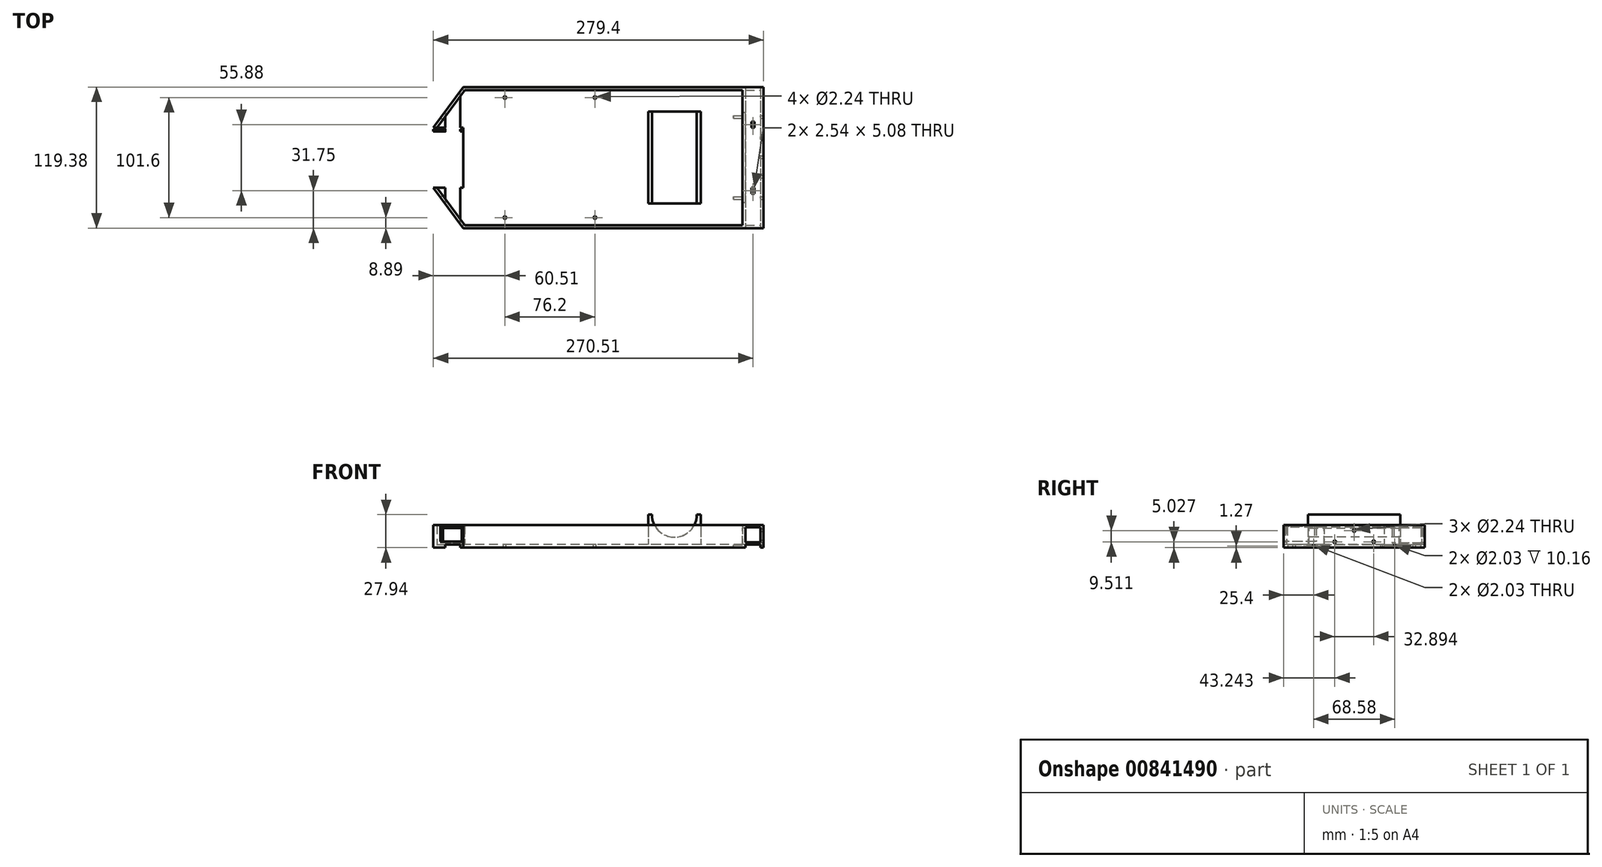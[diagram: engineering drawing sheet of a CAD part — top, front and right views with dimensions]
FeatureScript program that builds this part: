
annotation { "Feature Type Name" : "Feature", "Feature Type Description" : "" }
export const myFeature = defineFeature(function(context is Context, id is Id, definition is map)
    precondition{}
    {
        {
            var Q0;
            Q0=qCreatedBy(makeId("Top.planeOp"),FACE);
            var sketch = newSketch(context, id + "F0", { "sketchPlane" : qUnion([Q0])});
            skLineSegment(sketch, "E0.bottom", {"start": v(127, -59.69) * mm, "end": v(-127, -59.7) * mm});
            skLineSegment(sketch, "E0.top", {"start": v(127, 59.7) * mm, "end": v(-127, 59.69) * mm});
            skLineSegment(sketch, "E0.left", {"start": v(127, -59.69) * mm, "end": v(127, 59.7) * mm});
            skLineSegment(sketch, "E0.right", {"start": v(-127, -59.7) * mm, "end": v(-127, 59.69) * mm});
            skPoint(sketch, "E0.middle", {"position": v(0, 0) * mm});
            skLineSegment(sketch, "E1", {"start": v(-152.4, 25.4) * mm, "end": v(-152.4, -25.4) * mm});
            skLineSegment(sketch, "E2", {"start": v(-152.4, 25.4) * mm, "end": v(-127, 59.69) * mm});
            skLineSegment(sketch, "E3", {"start": v(-152.4, -25.4) * mm, "end": v(-127, -59.7) * mm});
            skSolve(sketch);
        }
        {
            var Q0;
            Q0 = qSketchRegion(id + "F0", true);
            extrude(context, id + "F1", {"entities" : qUnion([Q0]), "depth" : 19.05 * mm, "offsetDistance" : 25.4 * mm});
        }
        {
            var Q0;
            Q0=makeQuery(id+"F1.opExtrude","CAP_FACE",FACE,{"disambiguationData":[OSD([sQuery(id+"F0.wireOp",EDGE,"E0.bottom"),sQuery(id+"F0.wireOp",EDGE,"E0.top"),sQuery(id+"F0.wireOp",EDGE,"E0.left"),sQuery(id+"F0.wireOp",EDGE,"E1"),sQuery(id+"F0.wireOp",EDGE,"E2"),sQuery(id+"F0.wireOp",EDGE,"E3")])],"isStart":false});
            shell(context, id + "F2", {"entities" : qUnion([Q0]), "thickness" : 2.54 * mm});
        }
        {
            var Q0;
            Q0=makeQuery(id+"F1.opExtrude","SWEPT_FACE",FACE,{"disambiguationData":[OSD([sQuery(id+"F0.wireOp",EDGE,"E3")])]});
            var sketch = newSketch(context, id + "F3", { "sketchPlane" : qUnion([Q0])});
            skLineSegment(sketch, "E4.bottom", {"start": v(-60.14, 17.78) * mm, "end": v(-29.66, 17.78) * mm});
            skLineSegment(sketch, "E4.top", {"start": v(-60.14, 5.08) * mm, "end": v(-29.66, 5.08) * mm});
            skLineSegment(sketch, "E4.left", {"start": v(-60.14, 17.78) * mm, "end": v(-60.14, 5.08) * mm});
            skLineSegment(sketch, "E4.right", {"start": v(-29.66, 17.78) * mm, "end": v(-29.66, 5.08) * mm});
            skSolve(sketch);
        }
        {
            var Q0;
            Q0 = qSketchRegion(id + "F3", true);
            extrude(context, id + "F4", {"entities" : qUnion([Q0]), "operationType" : NewBodyOperationType.REMOVE, "oppositeDirection" : true, "depth" : 2.54 * mm, "offsetDistance" : 25.4 * mm});
        }
        {
            var Q0;
            Q0=makeQuery(id+"F1.opExtrude","CAP_FACE",FACE,{"disambiguationData":[OSD([sQuery(id+"F0.wireOp",EDGE,"E0.bottom"),sQuery(id+"F0.wireOp",EDGE,"E0.top"),sQuery(id+"F0.wireOp",EDGE,"E0.left"),sQuery(id+"F0.wireOp",EDGE,"E1"),sQuery(id+"F0.wireOp",EDGE,"E2"),sQuery(id+"F0.wireOp",EDGE,"E3")])],"isStart":true});
            var sketch = newSketch(context, id + "F5", { "sketchPlane" : qUnion([Q0])});
            skLineSegment(sketch, "E5", {"start": v(-129.54, 56.26) * mm, "end": v(-129.54, -56.26) * mm});
            skLineSegment(sketch, "E6", {"start": v(-142.24, -39.12) * mm, "end": v(-142.24, 39.12) * mm});
            skLineSegment(sketch, "E7", {"start": v(-129.54, -56.26) * mm, "end": v(-142.24, -39.12) * mm});
            skLineSegment(sketch, "E8", {"start": v(-142.24, 39.12) * mm, "end": v(-129.54, 56.26) * mm});
            skLineSegment(sketch, "E9.bottom", {"start": v(124.46, -59.7) * mm, "end": v(111.76, -59.7) * mm});
            skLineSegment(sketch, "E9.top", {"start": v(124.46, 59.7) * mm, "end": v(111.76, 59.69) * mm});
            skLineSegment(sketch, "E9.left", {"start": v(124.46, -59.7) * mm, "end": v(124.46, 59.7) * mm});
            skLineSegment(sketch, "E9.right", {"start": v(111.76, -59.7) * mm, "end": v(111.76, 59.69) * mm});
            skSolve(sketch);
        }
        {
            var Q0;
            Q0=makeQuery(id+"F5.imprint","IMPRINT",FACE,{"disambiguationData":[TD([[makeQuery(id+"F5.imprint","IMPRINT",EDGE,{"derivedFrom":sQuery(id+"F5.wireOp",EDGE,"E5")}),-1.0]])]});
            var Q1;
            Q1=makeQuery(id+"F5.imprint","IMPRINT",FACE,{"disambiguationData":[TD([[makeQuery(id+"F5.imprint","IMPRINT",EDGE,{"derivedFrom":sQuery(id+"F5.wireOp",EDGE,"E9.bottom")}),-1.0]])]});
            extrude(context, id + "F6", {"entities" : qUnion([Q0, Q1]), "operationType" : NewBodyOperationType.REMOVE, "oppositeDirection" : true, "depth" : 2.54 * mm, "offsetDistance" : 25.4 * mm});
        }
        {
            var Q0;
            Q0=makeQuery(id+"F1.opExtrude","SWEPT_FACE",FACE,{"disambiguationData":[OSD([sQuery(id+"F0.wireOp",EDGE,"E1")])]});
            var sketch = newSketch(context, id + "F7", { "sketchPlane" : qUnion([Q0])});
            skCircle(sketch, "E10", {"center": v(23.11, 1.27) * mm, "radius": 1.02 * mm});
            skCircle(sketch, "E11.MirrorC", {"center": v(-23.11, 1.27) * mm, "radius": 1.02 * mm});
            skSolve(sketch);
        }
        {
            var Q0;
            Q0=makeQuery(id+"F7.imprint","IMPRINT",FACE,{"disambiguationData":[TD([[makeQuery(id+"F7.imprint","IMPRINT",EDGE,{"derivedFrom":sQuery(id+"F7.wireOp",EDGE,"E11.MirrorC")}),-1.0]])]});
            var Q1;
            Q1=makeQuery(id+"F7.imprint","IMPRINT",FACE,{"disambiguationData":[TD([[makeQuery(id+"F7.imprint","IMPRINT",EDGE,{"derivedFrom":sQuery(id+"F7.wireOp",EDGE,"E10")}),1.0]])]});
            extrude(context, id + "F8", {"entities" : qUnion([Q0, Q1]), "operationType" : NewBodyOperationType.REMOVE, "oppositeDirection" : true, "depth" : 25.4 * mm, "offsetDistance" : 25.4 * mm});
        }
        {
            var Q0;
            Q0=makeQuery(id+"F1.opExtrude","SWEPT_FACE",FACE,{"disambiguationData":[OSD([sQuery(id+"F0.wireOp",EDGE,"E0.left")])]});
            var sketch = newSketch(context, id + "F9", { "sketchPlane" : qUnion([Q0])});
            skCircle(sketch, "E12", {"center": v(-34.29, 1.27) * mm, "radius": 1.02 * mm});
            skCircle(sketch, "E13.MirrorC", {"center": v(34.29, 1.27) * mm, "radius": 1.02 * mm});
            skSolve(sketch);
        }
        {
            var Q0;
            Q0 = qSketchRegion(id + "F9", true);
            extrude(context, id + "F10", {"entities" : qUnion([Q0]), "operationType" : NewBodyOperationType.REMOVE, "oppositeDirection" : true, "depth" : 25.4 * mm, "offsetDistance" : 25.4 * mm});
        }
        {
            var Q0;
            Q0=makeQuery(id+"F1.opExtrude","SWEPT_FACE",FACE,{"disambiguationData":[OSD([sQuery(id+"F0.wireOp",EDGE,"E2")])]});
            var sketch = newSketch(context, id + "F11", { "sketchPlane" : qUnion([Q0])});
            skLineSegment(sketch, "E14.bottom", {"start": v(29.66, 16.51) * mm, "end": v(60.14, 16.51) * mm});
            skLineSegment(sketch, "E14.top", {"start": v(29.66, 3.81) * mm, "end": v(60.14, 3.81) * mm});
            skLineSegment(sketch, "E14.left", {"start": v(29.66, 16.51) * mm, "end": v(29.66, 3.81) * mm});
            skLineSegment(sketch, "E14.right", {"start": v(60.14, 16.51) * mm, "end": v(60.14, 3.81) * mm});
            skSolve(sketch);
        }
        {
            var Q0;
            Q0 = qSketchRegion(id + "F11", true);
            extrude(context, id + "F12", {"entities" : qUnion([Q0]), "operationType" : NewBodyOperationType.REMOVE, "oppositeDirection" : true, "depth" : 2.54 * mm, "offsetDistance" : 25.4 * mm});
        }
        {
            var Q0;
            Q0=makeQuery(id+"F1.opExtrude","SWEPT_FACE",FACE,{"disambiguationData":[OSD([sQuery(id+"F0.wireOp",EDGE,"E0.bottom")])]});
            var sketch = newSketch(context, id + "F13", { "sketchPlane" : qUnion([Q0])});
            skLineSegment(sketch, "E15.bottom", {"start": v(111.76, 4.45) * mm, "end": v(124.46, 4.45) * mm});
            skLineSegment(sketch, "E15.top", {"start": v(111.76, 17.14) * mm, "end": v(124.46, 17.14) * mm});
            skLineSegment(sketch, "E15.left", {"start": v(111.76, 4.45) * mm, "end": v(111.76, 17.15) * mm});
            skLineSegment(sketch, "E15.right", {"start": v(124.46, 4.45) * mm, "end": v(124.46, 17.14) * mm});
            skSolve(sketch);
        }
        {
            var Q0;
            Q0 = qSketchRegion(id + "F13", true);
            extrude(context, id + "F14", {"entities" : qUnion([Q0]), "operationType" : NewBodyOperationType.REMOVE, "oppositeDirection" : true, "depth" : 101.6 * mm, "offsetDistance" : 25.4 * mm});
        }
        {
            var Q0;
            Q0=qCreatedBy(makeId("Right.planeOp"),FACE);
            var sketch = newSketch(context, id + "F15", { "sketchPlane" : qUnion([Q0])});
            skCircle(sketch, "E16", {"center": v(0, 11.81) * mm, "radius": 1.12 * mm});
            skCircle(sketch, "E17", {"center": v(-17.78, 5.08) * mm, "radius": 1.12 * mm});
            skCircle(sketch, "E18", {"center": v(17.78, 5.08) * mm, "radius": 1.12 * mm});
            skSolve(sketch);
        }
        {
            var Q0;
            Q0 = qSketchRegion(id + "F15", true);
            extrude(context, id + "F16", {"entities" : qUnion([Q0]), "operationType" : NewBodyOperationType.REMOVE, "endBound" : BoundingType.SYMMETRIC, "oppositeDirection" : true, "depth" : 169.16 * mm, "offsetDistance" : 25.4 * mm});
        }
        {
            var Q0;
            Q0=makeQuery(id+"F1.opExtrude","SWEPT_FACE",FACE,{"disambiguationData":[OSD([sQuery(id+"F0.wireOp",EDGE,"E1")])]});
            var sketch = newSketch(context, id + "F17", { "sketchPlane" : qUnion([Q0])});
            skCircle(sketch, "E19", {"center": v(-16.45, 5.03) * mm, "radius": 1.12 * mm});
            skCircle(sketch, "E20", {"center": v(16.45, 5.03) * mm, "radius": 1.12 * mm});
            skCircle(sketch, "E21", {"center": v(0, 14.54) * mm, "radius": 1.12 * mm});
            skSolve(sketch);
        }
        {
            var Q0;
            Q0 = qSketchRegion(id + "F17", true);
            extrude(context, id + "F18", {"entities" : qUnion([Q0]), "operationType" : NewBodyOperationType.REMOVE, "oppositeDirection" : true, "depth" : 279.4 * mm, "offsetDistance" : 25.4 * mm});
        }
        {
            var Q0;
            {var subQ0=sQuery(id+"F0.wireOp",EDGE,"E3");var subQ3=sQuery(id+"F0.wireOp",EDGE,"E0.top");var subQ4=sQuery(id+"F0.wireOp",EDGE,"E2");var subQ5=sQuery(id+"F0.wireOp",EDGE,"E0.bottom");Q0=makeQuery(id+"F6.boolean.opBoolean","SPLIT",FACE,{"disambiguationData":[TD([makeQuery(id+"F2.opShell","OFFSET_FACE",FACE,{"disambiguationData":[OSD([subQ5])]})])],"derivedFrom":makeQuery(id+"F2.opShell","OFFSET_FACE",FACE,{"disambiguationData":[OSD([subQ5,subQ3,sQuery(id+"F0.wireOp",EDGE,"E0.left"),sQuery(id+"F0.wireOp",EDGE,"E1"),subQ4,subQ0])]})});}
            var sketch = newSketch(context, id + "F19", { "sketchPlane" : qUnion([Q0])});
            skLineSegment(sketch, "E22.bottom", {"start": v(-15.7, -50.8) * mm, "end": v(-91.9, -50.8) * mm});
            skLineSegment(sketch, "E22.top", {"start": v(-15.7, 50.8) * mm, "end": v(-91.9, 50.8) * mm});
            skLineSegment(sketch, "E22.left", {"start": v(-15.7, -50.8) * mm, "end": v(-15.7, 50.8) * mm});
            skLineSegment(sketch, "E22.right", {"start": v(-91.9, -50.8) * mm, "end": v(-91.9, 50.8) * mm});
            skPoint(sketch, "E22.middle", {"position": v(-53.8, 0) * mm});
            skCircle(sketch, "E23", {"center": v(-91.9, 50.8) * mm, "radius": 1.12 * mm});
            skCircle(sketch, "E24", {"center": v(-15.7, 50.8) * mm, "radius": 1.12 * mm});
            skCircle(sketch, "E25", {"center": v(-15.7, -50.8) * mm, "radius": 1.12 * mm});
            skCircle(sketch, "E26", {"center": v(-91.9, -50.8) * mm, "radius": 1.12 * mm});
            skSolve(sketch);
        }
        {
            var Q0;
            {var subQ0=sQuery(id+"F19.wireOp",EDGE,"E22.right");var subQ1=sQuery(id+"F19.wireOp",EDGE,"E22.bottom");var subQ2=makeQuery(id+"F19.imprint","INTERSECT",VERTEX,{"derivedFrom":[subQ1,subQ0]});Q0=makeQuery(id+"F19.imprint","IMPRINT",FACE,{"disambiguationData":[TD([[makeQuery(id+"F19.imprint","IMPRINT",EDGE,{"disambiguationData":[TD([[subQ2,1.0]])],"derivedFrom":subQ1}),-1.0]])]});}
            var Q1;
            {var subQ0=sQuery(id+"F19.wireOp",EDGE,"E22.right");var subQ1=sQuery(id+"F19.wireOp",EDGE,"E22.bottom");var subQ2=makeQuery(id+"F19.imprint","INTERSECT",VERTEX,{"derivedFrom":[subQ1,subQ0]});Q1=makeQuery(id+"F19.imprint","IMPRINT",FACE,{"disambiguationData":[TD([[makeQuery(id+"F19.imprint","IMPRINT",EDGE,{"disambiguationData":[TD([[subQ2,1.0]])],"derivedFrom":subQ1}),1.0]])]});}
            var Q2;
            {var subQ0=sQuery(id+"F19.wireOp",EDGE,"E22.left");var subQ1=sQuery(id+"F19.wireOp",EDGE,"E22.bottom");var subQ2=makeQuery(id+"F19.imprint","INTERSECT",VERTEX,{"derivedFrom":[subQ1,subQ0]});Q2=makeQuery(id+"F19.imprint","IMPRINT",FACE,{"disambiguationData":[TD([[makeQuery(id+"F19.imprint","IMPRINT",EDGE,{"disambiguationData":[TD([[subQ2,-1.0]])],"derivedFrom":subQ1}),1.0]])]});}
            var Q3;
            {var subQ0=sQuery(id+"F19.wireOp",EDGE,"E22.left");var subQ1=sQuery(id+"F19.wireOp",EDGE,"E22.bottom");var subQ2=makeQuery(id+"F19.imprint","INTERSECT",VERTEX,{"derivedFrom":[subQ1,subQ0]});Q3=makeQuery(id+"F19.imprint","IMPRINT",FACE,{"disambiguationData":[TD([[makeQuery(id+"F19.imprint","IMPRINT",EDGE,{"disambiguationData":[TD([[subQ2,-1.0]])],"derivedFrom":subQ1}),-1.0]])]});}
            var Q4;
            {var subQ0=sQuery(id+"F19.wireOp",EDGE,"E22.left");var subQ1=sQuery(id+"F19.wireOp",EDGE,"E22.top");var subQ2=makeQuery(id+"F19.imprint","INTERSECT",VERTEX,{"derivedFrom":[subQ1,subQ0]});Q4=makeQuery(id+"F19.imprint","IMPRINT",FACE,{"disambiguationData":[TD([[makeQuery(id+"F19.imprint","IMPRINT",EDGE,{"disambiguationData":[TD([[subQ2,-1.0]])],"derivedFrom":subQ1}),-1.0]])]});}
            var Q5;
            {var subQ0=sQuery(id+"F19.wireOp",EDGE,"E22.left");var subQ1=sQuery(id+"F19.wireOp",EDGE,"E22.top");var subQ2=makeQuery(id+"F19.imprint","INTERSECT",VERTEX,{"derivedFrom":[subQ1,subQ0]});Q5=makeQuery(id+"F19.imprint","IMPRINT",FACE,{"disambiguationData":[TD([[makeQuery(id+"F19.imprint","IMPRINT",EDGE,{"disambiguationData":[TD([[subQ2,-1.0]])],"derivedFrom":subQ1}),1.0]])]});}
            var Q6;
            {var subQ0=sQuery(id+"F19.wireOp",EDGE,"E22.right");var subQ1=sQuery(id+"F19.wireOp",EDGE,"E22.top");var subQ2=makeQuery(id+"F19.imprint","INTERSECT",VERTEX,{"derivedFrom":[subQ1,subQ0]});Q6=makeQuery(id+"F19.imprint","IMPRINT",FACE,{"disambiguationData":[TD([[makeQuery(id+"F19.imprint","IMPRINT",EDGE,{"disambiguationData":[TD([[subQ2,1.0]])],"derivedFrom":subQ1}),-1.0]])]});}
            var Q7;
            {var subQ0=sQuery(id+"F19.wireOp",EDGE,"E22.right");var subQ1=sQuery(id+"F19.wireOp",EDGE,"E22.top");var subQ2=makeQuery(id+"F19.imprint","INTERSECT",VERTEX,{"derivedFrom":[subQ1,subQ0]});Q7=makeQuery(id+"F19.imprint","IMPRINT",FACE,{"disambiguationData":[TD([[makeQuery(id+"F19.imprint","IMPRINT",EDGE,{"disambiguationData":[TD([[subQ2,1.0]])],"derivedFrom":subQ1}),1.0]])]});}
            extrude(context, id + "F20", {"entities" : qUnion([Q0, Q1, Q2, Q3, Q4, Q5, Q6, Q7]), "operationType" : NewBodyOperationType.REMOVE, "oppositeDirection" : true, "depth" : 2.54 * mm, "offsetDistance" : 25.4 * mm});
        }
        {
            var Q0;
            {var subQ0=sQuery(id+"F0.wireOp",EDGE,"E3");var subQ3=sQuery(id+"F0.wireOp",EDGE,"E0.top");var subQ4=sQuery(id+"F0.wireOp",EDGE,"E2");var subQ5=sQuery(id+"F0.wireOp",EDGE,"E0.bottom");Q0=makeQuery(id+"F6.boolean.opBoolean","SPLIT",FACE,{"disambiguationData":[TD([makeQuery(id+"F2.opShell","OFFSET_FACE",FACE,{"disambiguationData":[OSD([subQ5])]})])],"derivedFrom":makeQuery(id+"F2.opShell","OFFSET_FACE",FACE,{"disambiguationData":[OSD([subQ5,subQ3,sQuery(id+"F0.wireOp",EDGE,"E0.left"),sQuery(id+"F0.wireOp",EDGE,"E1"),subQ4,subQ0])]})});}
            var sketch = newSketch(context, id + "F21", { "sketchPlane" : qUnion([Q0])});
            skLineSegment(sketch, "E27.bottom", {"start": v(73.76, -38.99) * mm, "end": v(29.31, -38.99) * mm});
            skLineSegment(sketch, "E27.top", {"start": v(73.76, 38.99) * mm, "end": v(29.31, 38.99) * mm});
            skLineSegment(sketch, "E27.left", {"start": v(73.76, -38.99) * mm, "end": v(73.76, 38.99) * mm});
            skLineSegment(sketch, "E27.right", {"start": v(29.31, -38.99) * mm, "end": v(29.31, 38.99) * mm});
            skPoint(sketch, "E27.middle", {"position": v(51.54, 0) * mm});
            skSolve(sketch);
        }
        {
            var Q0;
            Q0 = qSketchRegion(id + "F21", true);
            extrude(context, id + "F22", {"entities" : qUnion([Q0]), "operationType" : NewBodyOperationType.ADD, "depth" : 25.4 * mm, "offsetDistance" : 25.4 * mm});
        }
        {
            var Q0;
            Q0=makeQuery(id+"F22.opExtrude","SWEPT_FACE",FACE,{"disambiguationData":[OSD([sQuery(id+"F21.wireOp",EDGE,"E27.bottom")])]});
            var sketch = newSketch(context, id + "F23", { "sketchPlane" : qUnion([Q0])});
            skCircle(sketch, "E28", {"center": v(51.54, 27.94) * mm, "radius": 19 * mm});
            skSolve(sketch);
        }
        {
            var Q0;
            Q0 = qSketchRegion(id + "F23", true);
            extrude(context, id + "F24", {"entities" : qUnion([Q0]), "operationType" : NewBodyOperationType.REMOVE, "oppositeDirection" : true, "depth" : 77.98 * mm, "offsetDistance" : 25.4 * mm});
        }
        {
            var Q0;
            Q0=makeQuery(id+"F14.boolean.opBoolean","MERGE",FACE,{"derivedFrom":[makeQuery(id+"F6.boolean.opBoolean","MERGE",FACE,{"derivedFrom":[makeQuery(id+"F2.opShell","OFFSET_FACE",FACE,{"disambiguationData":[OSD([sQuery(id+"F0.wireOp",EDGE,"E0.left")])]}),makeQuery(id+"F6.opExtrude","SWEPT_FACE",FACE,{"disambiguationData":[OSD([sQuery(id+"F5.wireOp",EDGE,"E9.left")])]})]}),makeQuery(id+"F14.opExtrude","SWEPT_FACE",FACE,{"disambiguationData":[OSD([sQuery(id+"F13.wireOp",EDGE,"E15.right")])]})]});
            var sketch = newSketch(context, id + "F25", { "sketchPlane" : qUnion([Q0])});
            skLineSegment(sketch, "E29.bottom", {"start": v(57.15, 19.05) * mm, "end": v(-57.15, 19.05) * mm});
            skLineSegment(sketch, "E29.top", {"start": v(57.15, 17.14) * mm, "end": v(-57.15, 17.14) * mm});
            skLineSegment(sketch, "E29.left", {"start": v(57.15, 19.05) * mm, "end": v(57.15, 17.15) * mm});
            skLineSegment(sketch, "E29.right", {"start": v(-57.15, 19.05) * mm, "end": v(-57.15, 17.14) * mm});
            skSolve(sketch);
        }
        {
            var Q0;
            Q0 = qSketchRegion(id + "F25", true);
            extrude(context, id + "F26", {"entities" : qUnion([Q0]), "operationType" : NewBodyOperationType.ADD, "depth" : 12.7 * mm, "offsetDistance" : 25.4 * mm});
        }
        {
            var Q0;
            {var subQ0=sQuery(id+"F0.wireOp",EDGE,"E3");var subQ3=sQuery(id+"F0.wireOp",EDGE,"E0.top");var subQ4=sQuery(id+"F0.wireOp",EDGE,"E2");var subQ5=sQuery(id+"F0.wireOp",EDGE,"E0.bottom");Q0=makeQuery(id+"F6.boolean.opBoolean","SPLIT",FACE,{"disambiguationData":[TD([makeQuery(id+"F2.opShell","OFFSET_FACE",FACE,{"disambiguationData":[OSD([subQ5])]})])],"derivedFrom":makeQuery(id+"F2.opShell","OFFSET_FACE",FACE,{"disambiguationData":[OSD([subQ5,subQ3,sQuery(id+"F0.wireOp",EDGE,"E0.left"),sQuery(id+"F0.wireOp",EDGE,"E1"),subQ4,subQ0])]})});}
            var sketch = newSketch(context, id + "F27", { "sketchPlane" : qUnion([Q0])});
            skLineSegment(sketch, "E30.bottom", {"start": v(111.76, 57.15) * mm, "end": v(109.22, 57.15) * mm});
            skLineSegment(sketch, "E30.top", {"start": v(111.76, -57.15) * mm, "end": v(109.22, -57.15) * mm});
            skLineSegment(sketch, "E30.left", {"start": v(111.76, 57.15) * mm, "end": v(111.76, -57.15) * mm});
            skLineSegment(sketch, "E30.right", {"start": v(109.22, 57.15) * mm, "end": v(109.22, -57.15) * mm});
            skSolve(sketch);
        }
        {
            var Q0;
            Q0 = qSketchRegion(id + "F27", true);
            extrude(context, id + "F28", {"entities" : qUnion([Q0]), "operationType" : NewBodyOperationType.ADD, "depth" : 16.5 * mm, "offsetDistance" : 25.4 * mm});
        }
        {
            var Q0;
            Q0=makeQuery(id+"F28.boolean.opBoolean","MERGE",FACE,{"derivedFrom":[makeQuery(id+"F26.boolean.opBoolean","MERGE",FACE,{"derivedFrom":[makeQuery(id+"F1.opExtrude","CAP_FACE",FACE,{"disambiguationData":[OSD([sQuery(id+"F0.wireOp",EDGE,"E0.bottom"),sQuery(id+"F0.wireOp",EDGE,"E0.top"),sQuery(id+"F0.wireOp",EDGE,"E0.left"),sQuery(id+"F0.wireOp",EDGE,"E1"),sQuery(id+"F0.wireOp",EDGE,"E2"),sQuery(id+"F0.wireOp",EDGE,"E3")])],"isStart":false}),makeQuery(id+"F26.opExtrude","SWEPT_FACE",FACE,{"disambiguationData":[OSD([sQuery(id+"F25.wireOp",EDGE,"E29.bottom")])]})]}),makeQuery(id+"F28.opExtrude","CAP_FACE",FACE,{"disambiguationData":[OSD([sQuery(id+"F27.wireOp",EDGE,"E30.bottom"),sQuery(id+"F27.wireOp",EDGE,"E30.top"),sQuery(id+"F27.wireOp",EDGE,"E30.left"),sQuery(id+"F27.wireOp",EDGE,"E30.right")])],"isStart":false})]});
            var sketch = newSketch(context, id + "F29", { "sketchPlane" : qUnion([Q0])});
            skLineSegment(sketch, "E31.bottom", {"start": v(119.38, 30.48) * mm, "end": v(116.84, 30.48) * mm});
            skLineSegment(sketch, "E31.top", {"start": v(119.38, 25.4) * mm, "end": v(116.84, 25.4) * mm});
            skLineSegment(sketch, "E31.left", {"start": v(119.38, 30.48) * mm, "end": v(119.38, 25.4) * mm});
            skLineSegment(sketch, "E31.right", {"start": v(116.84, 30.48) * mm, "end": v(116.84, 25.4) * mm});
            skLineSegment(sketch, "E32.bottom", {"start": v(119.38, -30.48) * mm, "end": v(116.84, -30.48) * mm});
            skLineSegment(sketch, "E32.top", {"start": v(119.38, -25.4) * mm, "end": v(116.84, -25.4) * mm});
            skLineSegment(sketch, "E32.left", {"start": v(119.38, -30.48) * mm, "end": v(119.38, -25.4) * mm});
            skLineSegment(sketch, "E32.right", {"start": v(116.84, -30.48) * mm, "end": v(116.84, -25.4) * mm});
            skSolve(sketch);
        }
        {
            var Q0;
            Q0 = qSketchRegion(id + "F29", true);
            extrude(context, id + "F30", {"entities" : qUnion([Q0]), "operationType" : NewBodyOperationType.REMOVE, "oppositeDirection" : true, "depth" : 25.4 * mm, "offsetDistance" : 25.4 * mm});
        }
        {
            var Q0;
            Q0=makeQuery(id+"F28.opExtrude","SWEPT_FACE",FACE,{"disambiguationData":[OSD([sQuery(id+"F27.wireOp",EDGE,"E30.right")])]});
            var sketch = newSketch(context, id + "F31", { "sketchPlane" : qUnion([Q0])});
            skLineSegment(sketch, "E33.bottom", {"start": v(38.1, 2.54) * mm, "end": v(-38.1, 2.54) * mm});
            skLineSegment(sketch, "E33.top", {"start": v(38.1, 16.51) * mm, "end": v(-38.1, 16.51) * mm});
            skLineSegment(sketch, "E33.left", {"start": v(38.1, 2.54) * mm, "end": v(38.1, 16.51) * mm});
            skLineSegment(sketch, "E33.right", {"start": v(-38.1, 2.54) * mm, "end": v(-38.1, 16.51) * mm});
            skPoint(sketch, "E33.middle", {"position": v(0, 9.53) * mm});
            skPoint(sketch, "E33.middle.positionSnap0", {"position": v(0, 19.05) * mm});
            skPoint(sketch, "E33.centerSnap0", {"position": v(0, 19.05) * mm});
            skSolve(sketch);
        }
        {
            var Q0;
            Q0 = qSketchRegion(id + "F31", true);
            extrude(context, id + "F32", {"entities" : qUnion([Q0]), "operationType" : NewBodyOperationType.REMOVE, "oppositeDirection" : true, "depth" : 5.08 * mm, "offsetDistance" : 25.4 * mm});
        }
    });
